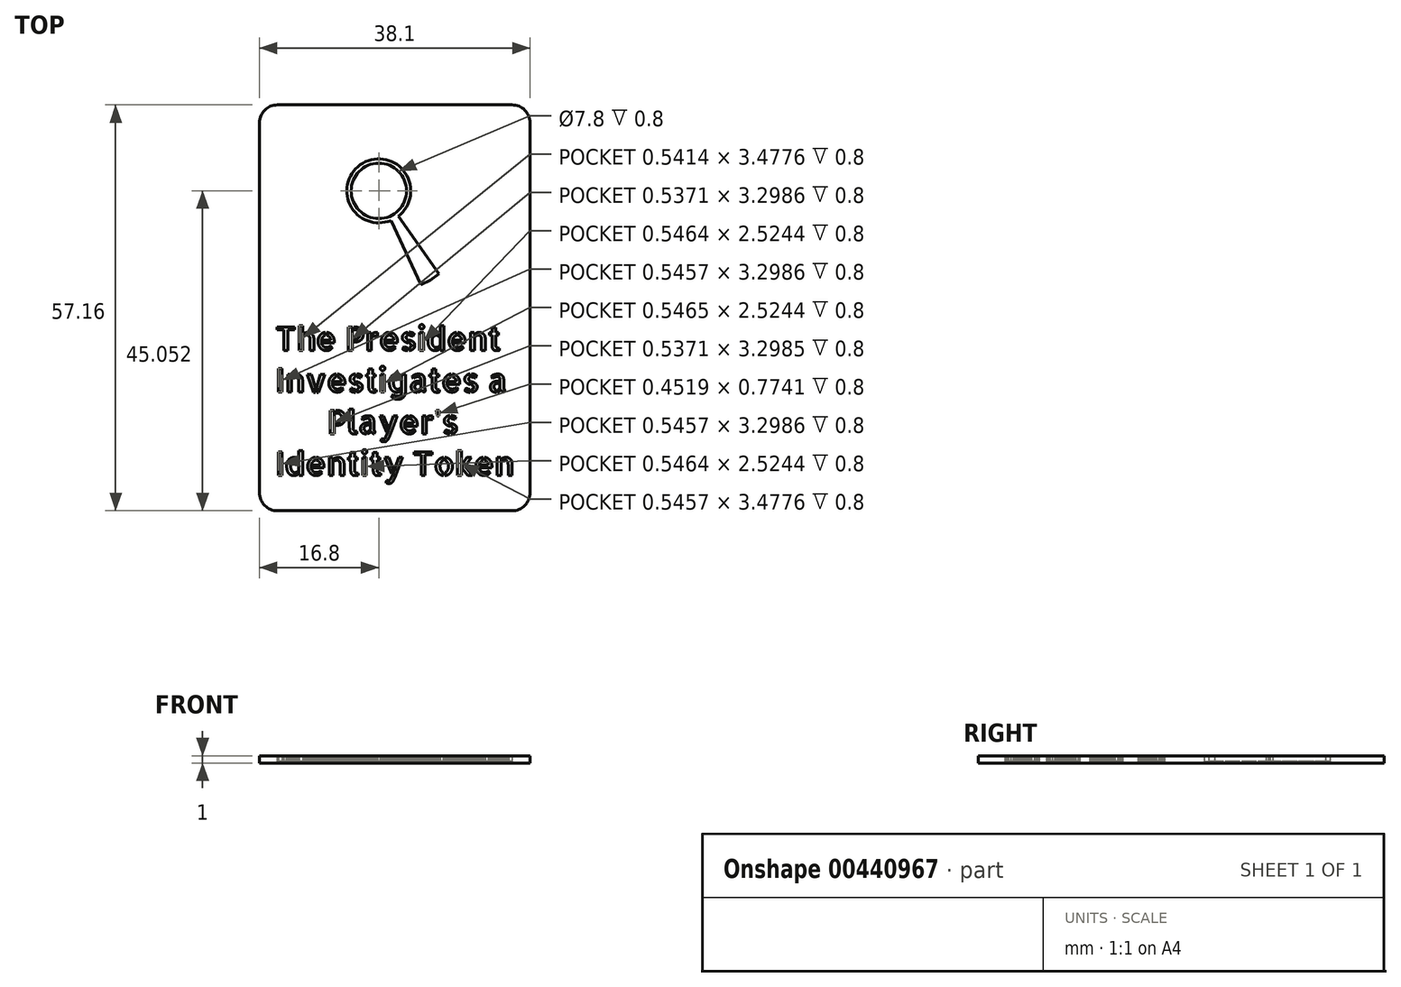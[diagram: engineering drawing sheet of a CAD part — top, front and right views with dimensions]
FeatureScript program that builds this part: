
annotation { "Feature Type Name" : "Feature", "Feature Type Description" : "" }
export const myFeature = defineFeature(function(context is Context, id is Id, definition is map)
    precondition{}
    {
        {
            var Q0;
            Q0=qCreatedBy(makeId("Top.planeOp"),FACE);
            var sketch = newSketch(context, id + "F0", { "sketchPlane" : qUnion([Q0])});
            skLineSegment(sketch, "E0.bottom", {"start": v(16.5, 28.58) * mm, "end": v(-16.51, 28.58) * mm});
            skLineSegment(sketch, "E0.top", {"start": v(16.51, -28.58) * mm, "end": v(-16.5, -28.58) * mm});
            skLineSegment(sketch, "E0.left", {"start": v(19.05, 26.04) * mm, "end": v(19.05, -26.04) * mm});
            skLineSegment(sketch, "E0.right", {"start": v(-19.05, 26.04) * mm, "end": v(-19.05, -26.04) * mm});
            skPoint(sketch, "E1.visualSharp", {"position": v(-19.05, 28.58) * mm});
            skArc(sketch, "E1.filletArc", {"start": v(-16.51, 28.58) * mm, "mid": v(-18.3, 27.83) * mm, "end": v(-19.05, 26.04) * mm});
            skPoint(sketch, "E2.visualSharp", {"position": v(19.05, 28.58) * mm});
            skArc(sketch, "E2.filletArc", {"start": v(19.05, 26.04) * mm, "mid": v(18.3, 27.83) * mm, "end": v(16.5, 28.58) * mm});
            skPoint(sketch, "E3.visualSharp", {"position": v(19.05, -28.58) * mm});
            skArc(sketch, "E3.filletArc", {"start": v(16.51, -28.58) * mm, "mid": v(18.3, -27.83) * mm, "end": v(19.05, -26.04) * mm});
            skPoint(sketch, "E4.visualSharp", {"position": v(-19.05, -28.58) * mm});
            skArc(sketch, "E4.filletArc", {"start": v(-19.05, -26.04) * mm, "mid": v(-18.3, -27.83) * mm, "end": v(-16.5, -28.58) * mm});
            skPoint(sketch, "E5", {"position": v(0, 12.58) * mm});
            skLineSegment(sketch, "E6", {"start": v(0, 12.58) * mm, "end": v(-19.05, 12.58) * mm, "construction": true});
            skLineSegment(sketch, "E7", {"start": v(0, 12.58) * mm, "end": v(19.05, 12.58) * mm, "construction": true});
            skLineSegment(sketch, "E8", {"start": v(0, 28.58) * mm, "end": v(0, 0) * mm, "construction": true});
            skLineSegment(sketch, "E9", {"start": v(0, 0) * mm, "end": v(0, -28.58) * mm, "construction": true});
            skCircle(sketch, "E10", {"center": v(-2.25, 16.47) * mm, "radius": 4.5 * mm});
            skCircle(sketch, "E11.0", {"center": v(-2.25, 16.47) * mm, "radius": 3.9 * mm});
            skLineSegment(sketch, "E12", {"start": v(-2.25, 16.47) * mm, "end": v(7.26, 0) * mm, "construction": true});
            skLineSegment(sketch, "E13", {"start": v(0.5, 12.9) * mm, "end": v(6.2, 4.76) * mm});
            skLineSegment(sketch, "E14", {"start": v(6.2, 4.76) * mm, "end": v(5, 3.91) * mm});
            skLineSegment(sketch, "E15.MirrorCS", {"start": v(-0.54, 12.31) * mm, "end": v(3.67, 3.3) * mm});
            skLineSegment(sketch, "E16.MirrorCS", {"start": v(3.67, 3.3) * mm, "end": v(5, 3.91) * mm});
            skText(sketch, "E17", { "text": "The President\nInvestigates a\n      Player\'s \nIdentity Token", "fontName": "AllertaStencil-Regular.ttf"});
            skLineSegment(sketch, "E18", {"start": v(-16.83, -2.7) * mm, "end": v(-19.05, -2.7) * mm, "construction": true});
            skLineSegment(sketch, "E19", {"start": v(16.83, -2.7) * mm, "end": v(19.05, -2.7) * mm, "construction": true});
            const initialGuessF0  = {"E17": [-0.01683, -0.006, 1, 0, 0.0033]};
            skSetInitialGuess(sketch, initialGuessF0);
            skSolve(sketch);
        }
        {
            var Q0;
            Q0=qSketchRegion(id+"F0",true);
            var Q1;
            Q1=makeQuery(id+"F0.imprint","IMPRINT",FACE,{"disambiguationData":[TD([[makeQuery(id+"F0.imprint","IMPRINT",EDGE,{"derivedFrom":sQuery(id+"F0.wireOp",EDGE,"1hngZ8Vo-O2Y1-8GoF-9924-SmxzgvlIe6eu")}),1.0]])]});
            var Q2;
            Q2=makeQuery(id+"F0.imprint","IMPRINT",FACE,{"disambiguationData":[TD([[makeQuery(id+"F0.imprint","IMPRINT",EDGE,{"derivedFrom":sQuery(id+"F0.wireOp",EDGE,"v3mnc92D-8hCO-dKtl-YXU8-LdhrgQy31VMY")}),1.0]])]});
            var Q3;
            Q3=makeQuery(id+"F0.imprint","IMPRINT",FACE,{"disambiguationData":[TD([[makeQuery(id+"F0.imprint","IMPRINT",EDGE,{"derivedFrom":sQuery(id+"F0.wireOp",EDGE,"XZppkLhH-C5au-Wygf-dwhr-iVVlCesrx2pO")}),1.0]])]});
            var Q4;
            Q4=makeQuery(id+"F0.imprint","IMPRINT",FACE,{"disambiguationData":[TD([[makeQuery(id+"F0.imprint","IMPRINT",EDGE,{"derivedFrom":sQuery(id+"F0.wireOp",EDGE,"y07g3fre-KKaQ-oYPB-yLvA-0BrsEIY3R70T")}),1.0]])]});
            var Q5;
            Q5=makeQuery(id+"F0.imprint","IMPRINT",FACE,{"disambiguationData":[TD([[makeQuery(id+"F0.imprint","IMPRINT",EDGE,{"derivedFrom":sQuery(id+"F0.wireOp",EDGE,"11e286c5-9b9c-43ac-b103-53d864957ac1.sketch_text.stroke-0")}),-1.0]])]});
            var Q6;
            Q6=makeQuery(id+"F0.imprint","IMPRINT",FACE,{"disambiguationData":[TD([[makeQuery(id+"F0.imprint","IMPRINT",EDGE,{"derivedFrom":sQuery(id+"F0.wireOp",EDGE,"11e286c5-9b9c-43ac-b103-53d864957ac1.sketch_text.stroke-8")}),-1.0]])]});
            var Q7;
            Q7=makeQuery(id+"F0.imprint","IMPRINT",FACE,{"disambiguationData":[TD([[makeQuery(id+"F0.imprint","IMPRINT",EDGE,{"derivedFrom":sQuery(id+"F0.wireOp",EDGE,"11e286c5-9b9c-43ac-b103-53d864957ac1.sketch_text.stroke-4")}),-1.0]])]});
            var Q8;
            Q8=makeQuery(id+"F0.imprint","IMPRINT",FACE,{"disambiguationData":[TD([[makeQuery(id+"F0.imprint","IMPRINT",EDGE,{"derivedFrom":sQuery(id+"F0.wireOp",EDGE,"11e286c5-9b9c-43ac-b103-53d864957ac1.sketch_text.stroke-31")}),-1.0]])]});
            var Q9;
            Q9=makeQuery(id+"F0.imprint","IMPRINT",FACE,{"disambiguationData":[TD([[makeQuery(id+"F0.imprint","IMPRINT",EDGE,{"derivedFrom":sQuery(id+"F0.wireOp",EDGE,"11e286c5-9b9c-43ac-b103-53d864957ac1.sketch_text.stroke-12")}),-1.0]])]});
            var Q10;
            Q10=makeQuery(id+"F0.imprint","IMPRINT",FACE,{"disambiguationData":[TD([[makeQuery(id+"F0.imprint","IMPRINT",EDGE,{"derivedFrom":sQuery(id+"F0.wireOp",EDGE,"11e286c5-9b9c-43ac-b103-53d864957ac1.sketch_text.stroke-96")}),-1.0]])]});
            var Q11;
            Q11=makeQuery(id+"F0.imprint","IMPRINT",FACE,{"disambiguationData":[TD([[makeQuery(id+"F0.imprint","IMPRINT",EDGE,{"derivedFrom":sQuery(id+"F0.wireOp",EDGE,"11e286c5-9b9c-43ac-b103-53d864957ac1.sketch_text.stroke-87")}),-1.0]])]});
            var Q12;
            Q12=makeQuery(id+"F0.imprint","IMPRINT",FACE,{"disambiguationData":[TD([[makeQuery(id+"F0.imprint","IMPRINT",EDGE,{"derivedFrom":sQuery(id+"F0.wireOp",EDGE,"11e286c5-9b9c-43ac-b103-53d864957ac1.sketch_text.stroke-67")}),-1.0]])]});
            var Q13;
            Q13=makeQuery(id+"F0.imprint","IMPRINT",FACE,{"disambiguationData":[TD([[makeQuery(id+"F0.imprint","IMPRINT",EDGE,{"derivedFrom":sQuery(id+"F0.wireOp",EDGE,"11e286c5-9b9c-43ac-b103-53d864957ac1.sketch_text.stroke-81")}),-1.0]])]});
            var Q14;
            Q14=makeQuery(id+"F0.imprint","IMPRINT",FACE,{"disambiguationData":[TD([[makeQuery(id+"F0.imprint","IMPRINT",EDGE,{"derivedFrom":sQuery(id+"F0.wireOp",EDGE,"11e286c5-9b9c-43ac-b103-53d864957ac1.sketch_text.stroke-116")}),-1.0]])]});
            var Q15;
            Q15=makeQuery(id+"F0.imprint","IMPRINT",FACE,{"disambiguationData":[TD([[makeQuery(id+"F0.imprint","IMPRINT",EDGE,{"derivedFrom":sQuery(id+"F0.wireOp",EDGE,"11e286c5-9b9c-43ac-b103-53d864957ac1.sketch_text.stroke-122")}),-1.0]])]});
            var Q16;
            Q16=makeQuery(id+"F0.imprint","IMPRINT",FACE,{"disambiguationData":[TD([[makeQuery(id+"F0.imprint","IMPRINT",EDGE,{"derivedFrom":sQuery(id+"F0.wireOp",EDGE,"11e286c5-9b9c-43ac-b103-53d864957ac1.sketch_text.stroke-110")}),-1.0]])]});
            var Q17;
            Q17=makeQuery(id+"F0.imprint","IMPRINT",FACE,{"disambiguationData":[TD([[makeQuery(id+"F0.imprint","IMPRINT",EDGE,{"derivedFrom":sQuery(id+"F0.wireOp",EDGE,"11e286c5-9b9c-43ac-b103-53d864957ac1.sketch_text.stroke-142")}),-1.0]])]});
            var Q18;
            Q18=makeQuery(id+"F0.imprint","IMPRINT",FACE,{"disambiguationData":[TD([[makeQuery(id+"F0.imprint","IMPRINT",EDGE,{"derivedFrom":sQuery(id+"F0.wireOp",EDGE,"11e286c5-9b9c-43ac-b103-53d864957ac1.sketch_text.stroke-138")}),-1.0]])]});
            var Q19;
            Q19=makeQuery(id+"F0.imprint","IMPRINT",FACE,{"disambiguationData":[TD([[makeQuery(id+"F0.imprint","IMPRINT",EDGE,{"derivedFrom":sQuery(id+"F0.wireOp",EDGE,"11e286c5-9b9c-43ac-b103-53d864957ac1.sketch_text.stroke-170")}),-1.0]])]});
            var Q20;
            Q20=makeQuery(id+"F0.imprint","IMPRINT",FACE,{"disambiguationData":[TD([[makeQuery(id+"F0.imprint","IMPRINT",EDGE,{"derivedFrom":sQuery(id+"F0.wireOp",EDGE,"11e286c5-9b9c-43ac-b103-53d864957ac1.sketch_text.stroke-179")}),-1.0]])]});
            var Q21;
            Q21=makeQuery(id+"F0.imprint","IMPRINT",FACE,{"disambiguationData":[TD([[makeQuery(id+"F0.imprint","IMPRINT",EDGE,{"derivedFrom":sQuery(id+"F0.wireOp",EDGE,"11e286c5-9b9c-43ac-b103-53d864957ac1.sketch_text.stroke-150")}),-1.0]])]});
            var Q22;
            Q22=makeQuery(id+"F0.imprint","IMPRINT",FACE,{"disambiguationData":[TD([[makeQuery(id+"F0.imprint","IMPRINT",EDGE,{"derivedFrom":sQuery(id+"F0.wireOp",EDGE,"11e286c5-9b9c-43ac-b103-53d864957ac1.sketch_text.stroke-164")}),-1.0]])]});
            var Q23;
            Q23=makeQuery(id+"F0.imprint","IMPRINT",FACE,{"disambiguationData":[TD([[makeQuery(id+"F0.imprint","IMPRINT",EDGE,{"derivedFrom":sQuery(id+"F0.wireOp",EDGE,"11e286c5-9b9c-43ac-b103-53d864957ac1.sketch_text.stroke-193")}),-1.0]])]});
            var Q24;
            Q24=makeQuery(id+"F0.imprint","IMPRINT",FACE,{"disambiguationData":[TD([[makeQuery(id+"F0.imprint","IMPRINT",EDGE,{"derivedFrom":sQuery(id+"F0.wireOp",EDGE,"3hOEF64v-dSEU-imgf-cV2M-oAy4Y8LvNKR4")}),1.0]])]});
            var Q25;
            Q25=makeQuery(id+"F0.imprint","IMPRINT",FACE,{"disambiguationData":[TD([[makeQuery(id+"F0.imprint","IMPRINT",EDGE,{"derivedFrom":sQuery(id+"F0.wireOp",EDGE,"d61e87b4-afbc-4eba-b1e1-6c312846f633.1.0.0")}),1.0]])]});
            var Q26;
            Q26=makeQuery(id+"F0.imprint","IMPRINT",FACE,{"disambiguationData":[TD([[makeQuery(id+"F0.imprint","IMPRINT",EDGE,{"derivedFrom":sQuery(id+"F0.wireOp",EDGE,"d61e87b4-afbc-4eba-b1e1-6c312846f633.2.0.0")}),1.0]])]});
            var Q27;
            Q27=makeQuery(id+"F0.imprint","IMPRINT",FACE,{"disambiguationData":[TD([[makeQuery(id+"F0.imprint","IMPRINT",EDGE,{"derivedFrom":sQuery(id+"F0.wireOp",EDGE,"d61e87b4-afbc-4eba-b1e1-6c312846f633.3.0.0")}),1.0]])]});
            var Q28;
            Q28=makeQuery(id+"F0.imprint","IMPRINT",FACE,{"disambiguationData":[TD([[makeQuery(id+"F0.imprint","IMPRINT",EDGE,{"derivedFrom":sQuery(id+"F0.wireOp",EDGE,"d61e87b4-afbc-4eba-b1e1-6c312846f633.4.0.0")}),1.0]])]});
            var Q29;
            Q29=makeQuery(id+"F0.imprint","IMPRINT",FACE,{"disambiguationData":[TD([[makeQuery(id+"F0.imprint","IMPRINT",EDGE,{"derivedFrom":sQuery(id+"F0.wireOp",EDGE,"d61e87b4-afbc-4eba-b1e1-6c312846f633.5.0.0")}),1.0]])]});
            var Q30;
            Q30=makeQuery(id+"F0.imprint","IMPRINT",FACE,{"disambiguationData":[TD([[makeQuery(id+"F0.imprint","IMPRINT",EDGE,{"derivedFrom":sQuery(id+"F0.wireOp",EDGE,"d61e87b4-afbc-4eba-b1e1-6c312846f633.6.0.0")}),1.0]])]});
            var Q31;
            Q31=makeQuery(id+"F0.imprint","IMPRINT",FACE,{"disambiguationData":[TD([[makeQuery(id+"F0.imprint","IMPRINT",EDGE,{"derivedFrom":sQuery(id+"F0.wireOp",EDGE,"d61e87b4-afbc-4eba-b1e1-6c312846f633.7.0.0")}),1.0]])]});
            var Q32;
            Q32=makeQuery(id+"F0.imprint","IMPRINT",FACE,{"disambiguationData":[TD([[makeQuery(id+"F0.imprint","IMPRINT",EDGE,{"derivedFrom":sQuery(id+"F0.wireOp",EDGE,"d61e87b4-afbc-4eba-b1e1-6c312846f633.8.0.0")}),1.0]])]});
            var Q33;
            Q33=makeQuery(id+"F0.imprint","IMPRINT",FACE,{"disambiguationData":[TD([[makeQuery(id+"F0.imprint","IMPRINT",EDGE,{"derivedFrom":sQuery(id+"F0.wireOp",EDGE,"d61e87b4-afbc-4eba-b1e1-6c312846f633.9.0.0")}),1.0]])]});
            var Q34;
            Q34=makeQuery(id+"F0.imprint","IMPRINT",FACE,{"disambiguationData":[TD([[makeQuery(id+"F0.imprint","IMPRINT",EDGE,{"derivedFrom":sQuery(id+"F0.wireOp",EDGE,"d61e87b4-afbc-4eba-b1e1-6c312846f633.10.0.0")}),1.0]])]});
            var Q35;
            Q35=makeQuery(id+"F0.imprint","IMPRINT",FACE,{"disambiguationData":[TD([[makeQuery(id+"F0.imprint","IMPRINT",EDGE,{"derivedFrom":sQuery(id+"F0.wireOp",EDGE,"d61e87b4-afbc-4eba-b1e1-6c312846f633.11.0.0")}),1.0]])]});
            var Q36;
            Q36=makeQuery(id+"F0.imprint","IMPRINT",FACE,{"disambiguationData":[TD([[makeQuery(id+"F0.imprint","IMPRINT",EDGE,{"derivedFrom":sQuery(id+"F0.wireOp",EDGE,"d61e87b4-afbc-4eba-b1e1-6c312846f633.12.0.0")}),1.0]])]});
            var Q37;
            Q37=makeQuery(id+"F0.imprint","IMPRINT",FACE,{"disambiguationData":[TD([[makeQuery(id+"F0.imprint","IMPRINT",EDGE,{"derivedFrom":sQuery(id+"F0.wireOp",EDGE,"d61e87b4-afbc-4eba-b1e1-6c312846f633.13.0.0")}),1.0]])]});
            var Q38;
            Q38=makeQuery(id+"F0.imprint","IMPRINT",FACE,{"disambiguationData":[TD([[makeQuery(id+"F0.imprint","IMPRINT",EDGE,{"derivedFrom":sQuery(id+"F0.wireOp",EDGE,"d61e87b4-afbc-4eba-b1e1-6c312846f633.14.0.0")}),1.0]])]});
            var Q39;
            Q39=makeQuery(id+"F0.imprint","IMPRINT",FACE,{"disambiguationData":[TD([[makeQuery(id+"F0.imprint","IMPRINT",EDGE,{"derivedFrom":sQuery(id+"F0.wireOp",EDGE,"d61e87b4-afbc-4eba-b1e1-6c312846f633.15.0.0")}),1.0]])]});
            var Q40;
            Q40=makeQuery(id+"F0.imprint","IMPRINT",FACE,{"disambiguationData":[TD([[makeQuery(id+"F0.imprint","IMPRINT",EDGE,{"derivedFrom":sQuery(id+"F0.wireOp",EDGE,"d61e87b4-afbc-4eba-b1e1-6c312846f633.16.0.0")}),1.0]])]});
            var Q41;
            Q41=makeQuery(id+"F0.imprint","IMPRINT",FACE,{"disambiguationData":[TD([[makeQuery(id+"F0.imprint","IMPRINT",EDGE,{"derivedFrom":sQuery(id+"F0.wireOp",EDGE,"d61e87b4-afbc-4eba-b1e1-6c312846f633.17.0.0")}),1.0]])]});
            var Q42;
            Q42=makeQuery(id+"F0.imprint","IMPRINT",FACE,{"disambiguationData":[TD([[makeQuery(id+"F0.imprint","IMPRINT",EDGE,{"derivedFrom":sQuery(id+"F0.wireOp",EDGE,"d61e87b4-afbc-4eba-b1e1-6c312846f633.18.0.0")}),1.0]])]});
            var Q43;
            Q43=makeQuery(id+"F0.imprint","IMPRINT",FACE,{"disambiguationData":[TD([[makeQuery(id+"F0.imprint","IMPRINT",EDGE,{"derivedFrom":sQuery(id+"F0.wireOp",EDGE,"d61e87b4-afbc-4eba-b1e1-6c312846f633.19.0.0")}),1.0]])]});
            var Q44;
            Q44=makeQuery(id+"F0.imprint","IMPRINT",FACE,{"disambiguationData":[TD([[makeQuery(id+"F0.imprint","IMPRINT",EDGE,{"derivedFrom":sQuery(id+"F0.wireOp",EDGE,"d61e87b4-afbc-4eba-b1e1-6c312846f633.20.0.0")}),1.0]])]});
            var Q45;
            Q45=makeQuery(id+"F0.imprint","IMPRINT",FACE,{"disambiguationData":[TD([[makeQuery(id+"F0.imprint","IMPRINT",EDGE,{"derivedFrom":sQuery(id+"F0.wireOp",EDGE,"d61e87b4-afbc-4eba-b1e1-6c312846f633.21.0.0")}),1.0]])]});
            var Q46;
            Q46=makeQuery(id+"F0.imprint","IMPRINT",FACE,{"disambiguationData":[TD([[makeQuery(id+"F0.imprint","IMPRINT",EDGE,{"derivedFrom":sQuery(id+"F0.wireOp",EDGE,"824da2b7-0e67-4436-b530-e222e440d070.sketch_text.stroke-0")}),-1.0]])]});
            var Q47;
            Q47=makeQuery(id+"F0.imprint","IMPRINT",FACE,{"disambiguationData":[TD([[makeQuery(id+"F0.imprint","IMPRINT",EDGE,{"derivedFrom":sQuery(id+"F0.wireOp",EDGE,"824da2b7-0e67-4436-b530-e222e440d070.sketch_text.stroke-15")}),-1.0]])]});
            var Q48;
            Q48=makeQuery(id+"F0.imprint","IMPRINT",FACE,{"disambiguationData":[TD([[makeQuery(id+"F0.imprint","IMPRINT",EDGE,{"derivedFrom":sQuery(id+"F0.wireOp",EDGE,"824da2b7-0e67-4436-b530-e222e440d070.sketch_text.stroke-32")}),-1.0]])]});
            var Q49;
            Q49=makeQuery(id+"F0.imprint","IMPRINT",FACE,{"disambiguationData":[TD([[makeQuery(id+"F0.imprint","IMPRINT",EDGE,{"derivedFrom":sQuery(id+"F0.wireOp",EDGE,"824da2b7-0e67-4436-b530-e222e440d070.sketch_text.stroke-54")}),-1.0]])]});
            var Q50;
            Q50=makeQuery(id+"F0.imprint","IMPRINT",FACE,{"disambiguationData":[TD([[makeQuery(id+"F0.imprint","IMPRINT",EDGE,{"derivedFrom":sQuery(id+"F0.wireOp",EDGE,"824da2b7-0e67-4436-b530-e222e440d070.sketch_text.stroke-50")}),-1.0]])]});
            var Q51;
            Q51=makeQuery(id+"F0.imprint","IMPRINT",FACE,{"disambiguationData":[TD([[makeQuery(id+"F0.imprint","IMPRINT",EDGE,{"derivedFrom":sQuery(id+"F0.wireOp",EDGE,"824da2b7-0e67-4436-b530-e222e440d070.sketch_text.stroke-58")}),-1.0]])]});
            var Q52;
            Q52=makeQuery(id+"F0.imprint","IMPRINT",FACE,{"disambiguationData":[TD([[makeQuery(id+"F0.imprint","IMPRINT",EDGE,{"derivedFrom":sQuery(id+"F0.wireOp",EDGE,"824da2b7-0e67-4436-b530-e222e440d070.sketch_text.stroke-75")}),-1.0]])]});
            var Q53;
            Q53=makeQuery(id+"F0.imprint","IMPRINT",FACE,{"disambiguationData":[TD([[makeQuery(id+"F0.imprint","IMPRINT",EDGE,{"derivedFrom":sQuery(id+"F0.wireOp",EDGE,"824da2b7-0e67-4436-b530-e222e440d070.sketch_text.stroke-79")}),-1.0]])]});
            var Q54;
            Q54=makeQuery(id+"F0.imprint","IMPRINT",FACE,{"disambiguationData":[TD([[makeQuery(id+"F0.imprint","IMPRINT",EDGE,{"derivedFrom":sQuery(id+"F0.wireOp",EDGE,"prHT7NwA-CJht-v5NG-W2o7-Xqmxs18joHLs.bottom")}),-1.0]])]});
            var Q55;
            Q55=makeQuery(id+"F0.imprint","IMPRINT",FACE,{"disambiguationData":[TD([[makeQuery(id+"F0.imprint","IMPRINT",EDGE,{"derivedFrom":sQuery(id+"F0.wireOp",EDGE,"loqv97KZ-vKno-A8WI-mPE9-OnQyIJFUs6ra.bottom")}),-1.0]])]});
            var Q56;
            Q56=makeQuery(id+"F0.imprint","IMPRINT",FACE,{"disambiguationData":[TD([[makeQuery(id+"F0.imprint","IMPRINT",EDGE,{"derivedFrom":sQuery(id+"F0.wireOp",EDGE,"IiW4FtL9-cIlY-GVfC-fHN8-Muj6rfwzQ4Nk.bottom")}),-1.0]])]});
            var Q57;
            Q57=makeQuery(id+"F0.imprint","IMPRINT",FACE,{"disambiguationData":[TD([[makeQuery(id+"F0.imprint","IMPRINT",EDGE,{"derivedFrom":sQuery(id+"F0.wireOp",EDGE,"hgyYalZY-fuKV-cGhY-Ue2A-NU4bW9GvdhIw.bottom")}),-1.0]])]});
            var Q58;
            Q58=makeQuery(id+"F0.imprint","IMPRINT",FACE,{"disambiguationData":[TD([[makeQuery(id+"F0.imprint","IMPRINT",EDGE,{"derivedFrom":sQuery(id+"F0.wireOp",EDGE,"7RaPNTs9-LwY4-UvGH-fbjw-P0gIc8EvOOef.bottom")}),-1.0]])]});
            var Q59;
            Q59=makeQuery(id+"F0.imprint","IMPRINT",FACE,{"disambiguationData":[TD([[makeQuery(id+"F0.imprint","IMPRINT",EDGE,{"derivedFrom":sQuery(id+"F0.wireOp",EDGE,"0Oy3iZBW-l60p-ye98-HsD0-8aETsZGMw3y6.bottom")}),-1.0]])]});
            var Q60;
            Q60=makeQuery(id+"F0.imprint","IMPRINT",FACE,{"disambiguationData":[TD([[makeQuery(id+"F0.imprint","IMPRINT",EDGE,{"derivedFrom":sQuery(id+"F0.wireOp",EDGE,"uO9PoV1c-vtol-dT46-PGAY-6wPjbnXBpNAn.bottom")}),-1.0]])]});
            var Q61;
            Q61=makeQuery(id+"F0.imprint","IMPRINT",FACE,{"disambiguationData":[TD([[makeQuery(id+"F0.imprint","IMPRINT",EDGE,{"derivedFrom":sQuery(id+"F0.wireOp",EDGE,"HzYubSo2-mYeH-qRyi-21AG-W6rulPkjMyM9.bottom")}),-1.0]])]});
            var Q62;
            Q62=makeQuery(id+"F0.imprint","IMPRINT",FACE,{"disambiguationData":[TD([[makeQuery(id+"F0.imprint","IMPRINT",EDGE,{"derivedFrom":sQuery(id+"F0.wireOp",EDGE,"E11.0")}),1.0]])]});
            extrude(context, id + "F1", {"entities" : qUnion([Q0, Q1, Q2, Q3, Q4, Q5, Q6, Q7, Q8, Q9, Q10, Q11, Q12, Q13, Q14, Q15, Q16, Q17, Q18, Q19, Q20, Q21, Q22, Q23, Q24, Q25, Q26, Q27, Q28, Q29, Q30, Q31, Q32, Q33, Q34, Q35, Q36, Q37, Q38, Q39, Q40, Q41, Q42, Q43, Q44, Q45, Q46, Q47, Q48, Q49, Q50, Q51, Q52, Q53, Q54, Q55, Q56, Q57, Q58, Q59, Q60, Q61, Q62]), "depth" : 1 * mm, "offsetDistance" : 25 * mm});
        }
        {
            var Q0;
            Q0=makeQuery(id+"F0.imprint","IMPRINT",FACE,{"disambiguationData":[TD([[makeQuery(id+"F0.imprint","IMPRINT",EDGE,{"derivedFrom":sQuery(id+"F0.wireOp",EDGE,"E17.sketch_text.stroke-200")}),-1.0]])]});
            var Q1;
            Q1=makeQuery(id+"F0.imprint","IMPRINT",FACE,{"disambiguationData":[TD([[makeQuery(id+"F0.imprint","IMPRINT",EDGE,{"derivedFrom":sQuery(id+"F0.wireOp",EDGE,"E17.sketch_text.stroke-192")}),-1.0]])]});
            var Q2;
            Q2=makeQuery(id+"F0.imprint","IMPRINT",FACE,{"disambiguationData":[TD([[makeQuery(id+"F0.imprint","IMPRINT",EDGE,{"derivedFrom":sQuery(id+"F0.wireOp",EDGE,"E17.sketch_text.stroke-291")}),-1.0]])]});
            var Q3;
            {var subQ0=sQuery(id+"F0.wireOp",EDGE,"E13");Q3=makeQuery(id+"F0.imprint","IMPRINT",FACE,{"disambiguationData":[TD([[makeQuery(id+"F0.imprint","IMPRINT",EDGE,{"derivedFrom":subQ0}),-1.0]])]});}
            var Q4;
            Q4=makeQuery(id+"F0.imprint","IMPRINT",FACE,{"disambiguationData":[TD([[makeQuery(id+"F0.imprint","IMPRINT",EDGE,{"derivedFrom":sQuery(id+"F0.wireOp",EDGE,"E11.0")}),-1.0]])]});
            var Q5;
            Q5=makeQuery(id+"F0.imprint","IMPRINT",FACE,{"disambiguationData":[TD([[makeQuery(id+"F0.imprint","IMPRINT",EDGE,{"derivedFrom":sQuery(id+"F0.wireOp",EDGE,"E17.sketch_text.stroke-870")}),-1.0]])]});
            var Q6;
            Q6=makeQuery(id+"F0.imprint","IMPRINT",FACE,{"disambiguationData":[TD([[makeQuery(id+"F0.imprint","IMPRINT",EDGE,{"derivedFrom":sQuery(id+"F0.wireOp",EDGE,"E17.sketch_text.stroke-101")}),-1.0]])]});
            var Q7;
            Q7=makeQuery(id+"F0.imprint","IMPRINT",FACE,{"disambiguationData":[TD([[makeQuery(id+"F0.imprint","IMPRINT",EDGE,{"derivedFrom":sQuery(id+"F0.wireOp",EDGE,"E17.sketch_text.stroke-145")}),-1.0]])]});
            var Q8;
            Q8=makeQuery(id+"F0.imprint","IMPRINT",FACE,{"disambiguationData":[TD([[makeQuery(id+"F0.imprint","IMPRINT",EDGE,{"derivedFrom":sQuery(id+"F0.wireOp",EDGE,"E17.sketch_text.stroke-68")}),-1.0]])]});
            var Q9;
            Q9=makeQuery(id+"F0.imprint","IMPRINT",FACE,{"disambiguationData":[TD([[makeQuery(id+"F0.imprint","IMPRINT",EDGE,{"derivedFrom":sQuery(id+"F0.wireOp",EDGE,"E17.sketch_text.stroke-108")}),-1.0]])]});
            var Q10;
            Q10=makeQuery(id+"F0.imprint","IMPRINT",FACE,{"disambiguationData":[TD([[makeQuery(id+"F0.imprint","IMPRINT",EDGE,{"derivedFrom":sQuery(id+"F0.wireOp",EDGE,"E17.sketch_text.stroke-121")}),-1.0]])]});
            var Q11;
            Q11=makeQuery(id+"F0.imprint","IMPRINT",FACE,{"disambiguationData":[TD([[makeQuery(id+"F0.imprint","IMPRINT",EDGE,{"derivedFrom":sQuery(id+"F0.wireOp",EDGE,"E17.sketch_text.stroke-94")}),-1.0]])]});
            var Q12;
            Q12=makeQuery(id+"F0.imprint","IMPRINT",FACE,{"disambiguationData":[TD([[makeQuery(id+"F0.imprint","IMPRINT",EDGE,{"derivedFrom":sQuery(id+"F0.wireOp",EDGE,"E17.sketch_text.stroke-72")}),-1.0]])]});
            var Q13;
            Q13=makeQuery(id+"F0.imprint","IMPRINT",FACE,{"disambiguationData":[TD([[makeQuery(id+"F0.imprint","IMPRINT",EDGE,{"derivedFrom":sQuery(id+"F0.wireOp",EDGE,"E17.sketch_text.stroke-1079")}),-1.0]])]});
            var Q14;
            Q14=makeQuery(id+"F0.imprint","IMPRINT",FACE,{"disambiguationData":[TD([[makeQuery(id+"F0.imprint","IMPRINT",EDGE,{"derivedFrom":sQuery(id+"F0.wireOp",EDGE,"E17.sketch_text.stroke-205")}),-1.0]])]});
            var Q15;
            Q15=makeQuery(id+"F0.imprint","IMPRINT",FACE,{"disambiguationData":[TD([[makeQuery(id+"F0.imprint","IMPRINT",EDGE,{"derivedFrom":sQuery(id+"F0.wireOp",EDGE,"E17.sketch_text.stroke-941")}),-1.0]])]});
            var Q16;
            Q16=makeQuery(id+"F0.imprint","IMPRINT",FACE,{"disambiguationData":[TD([[makeQuery(id+"F0.imprint","IMPRINT",EDGE,{"derivedFrom":sQuery(id+"F0.wireOp",EDGE,"E17.sketch_text.stroke-792")}),-1.0]])]});
            var Q17;
            Q17=makeQuery(id+"F0.imprint","IMPRINT",FACE,{"disambiguationData":[TD([[makeQuery(id+"F0.imprint","IMPRINT",EDGE,{"derivedFrom":sQuery(id+"F0.wireOp",EDGE,"E17.sketch_text.stroke-1031")}),-1.0]])]});
            var Q18;
            Q18=makeQuery(id+"F0.imprint","IMPRINT",FACE,{"disambiguationData":[TD([[makeQuery(id+"F0.imprint","IMPRINT",EDGE,{"derivedFrom":sQuery(id+"F0.wireOp",EDGE,"E17.sketch_text.stroke-857")}),-1.0]])]});
            var Q19;
            Q19=makeQuery(id+"F0.imprint","IMPRINT",FACE,{"disambiguationData":[TD([[makeQuery(id+"F0.imprint","IMPRINT",EDGE,{"derivedFrom":sQuery(id+"F0.wireOp",EDGE,"E17.sketch_text.stroke-569")}),-1.0]])]});
            var Q20;
            Q20=makeQuery(id+"F0.imprint","IMPRINT",FACE,{"disambiguationData":[TD([[makeQuery(id+"F0.imprint","IMPRINT",EDGE,{"derivedFrom":sQuery(id+"F0.wireOp",EDGE,"E17.sketch_text.stroke-325")}),-1.0]])]});
            var Q21;
            Q21=makeQuery(id+"F0.imprint","IMPRINT",FACE,{"disambiguationData":[TD([[makeQuery(id+"F0.imprint","IMPRINT",EDGE,{"derivedFrom":sQuery(id+"F0.wireOp",EDGE,"E17.sketch_text.stroke-1050")}),-1.0]])]});
            var Q22;
            Q22=makeQuery(id+"F0.imprint","IMPRINT",FACE,{"disambiguationData":[TD([[makeQuery(id+"F0.imprint","IMPRINT",EDGE,{"derivedFrom":sQuery(id+"F0.wireOp",EDGE,"E17.sketch_text.stroke-594")}),-1.0]])]});
            var Q23;
            Q23=makeQuery(id+"F0.imprint","IMPRINT",FACE,{"disambiguationData":[TD([[makeQuery(id+"F0.imprint","IMPRINT",EDGE,{"derivedFrom":sQuery(id+"F0.wireOp",EDGE,"E17.sketch_text.stroke-344")}),-1.0]])]});
            var Q24;
            Q24=makeQuery(id+"F0.imprint","IMPRINT",FACE,{"disambiguationData":[TD([[makeQuery(id+"F0.imprint","IMPRINT",EDGE,{"derivedFrom":sQuery(id+"F0.wireOp",EDGE,"E17.sketch_text.stroke-1075")}),-1.0]])]});
            var Q25;
            Q25=makeQuery(id+"F0.imprint","IMPRINT",FACE,{"disambiguationData":[TD([[makeQuery(id+"F0.imprint","IMPRINT",EDGE,{"derivedFrom":sQuery(id+"F0.wireOp",EDGE,"E17.sketch_text.stroke-174")}),-1.0]])]});
            var Q26;
            Q26=makeQuery(id+"F0.imprint","IMPRINT",FACE,{"disambiguationData":[TD([[makeQuery(id+"F0.imprint","IMPRINT",EDGE,{"derivedFrom":sQuery(id+"F0.wireOp",EDGE,"E17.sketch_text.stroke-159")}),-1.0]])]});
            var Q27;
            Q27=makeQuery(id+"F0.imprint","IMPRINT",FACE,{"disambiguationData":[TD([[makeQuery(id+"F0.imprint","IMPRINT",EDGE,{"derivedFrom":sQuery(id+"F0.wireOp",EDGE,"E17.sketch_text.stroke-165")}),-1.0]])]});
            var Q28;
            Q28=makeQuery(id+"F0.imprint","IMPRINT",FACE,{"disambiguationData":[TD([[makeQuery(id+"F0.imprint","IMPRINT",EDGE,{"derivedFrom":sQuery(id+"F0.wireOp",EDGE,"E17.sketch_text.stroke-0")}),-1.0]])]});
            var Q29;
            Q29=makeQuery(id+"F0.imprint","IMPRINT",FACE,{"disambiguationData":[TD([[makeQuery(id+"F0.imprint","IMPRINT",EDGE,{"derivedFrom":sQuery(id+"F0.wireOp",EDGE,"E17.sketch_text.stroke-8")}),-1.0]])]});
            var Q30;
            Q30=makeQuery(id+"F0.imprint","IMPRINT",FACE,{"disambiguationData":[TD([[makeQuery(id+"F0.imprint","IMPRINT",EDGE,{"derivedFrom":sQuery(id+"F0.wireOp",EDGE,"E17.sketch_text.stroke-12")}),-1.0]])]});
            var Q31;
            Q31=makeQuery(id+"F0.imprint","IMPRINT",FACE,{"disambiguationData":[TD([[makeQuery(id+"F0.imprint","IMPRINT",EDGE,{"derivedFrom":sQuery(id+"F0.wireOp",EDGE,"E17.sketch_text.stroke-31")}),-1.0]])]});
            var Q32;
            Q32=makeQuery(id+"F0.imprint","IMPRINT",FACE,{"disambiguationData":[TD([[makeQuery(id+"F0.imprint","IMPRINT",EDGE,{"derivedFrom":sQuery(id+"F0.wireOp",EDGE,"E17.sketch_text.stroke-44")}),-1.0]])]});
            var Q33;
            Q33=makeQuery(id+"F0.imprint","IMPRINT",FACE,{"disambiguationData":[TD([[makeQuery(id+"F0.imprint","IMPRINT",EDGE,{"derivedFrom":sQuery(id+"F0.wireOp",EDGE,"E17.sketch_text.stroke-367")}),-1.0]])]});
            var Q34;
            Q34=makeQuery(id+"F0.imprint","IMPRINT",FACE,{"disambiguationData":[TD([[makeQuery(id+"F0.imprint","IMPRINT",EDGE,{"derivedFrom":sQuery(id+"F0.wireOp",EDGE,"E17.sketch_text.stroke-1112")}),-1.0]])]});
            var Q35;
            Q35=makeQuery(id+"F0.imprint","IMPRINT",FACE,{"disambiguationData":[TD([[makeQuery(id+"F0.imprint","IMPRINT",EDGE,{"derivedFrom":sQuery(id+"F0.wireOp",EDGE,"E17.sketch_text.stroke-645")}),-1.0]])]});
            var Q36;
            Q36=makeQuery(id+"F0.imprint","IMPRINT",FACE,{"disambiguationData":[TD([[makeQuery(id+"F0.imprint","IMPRINT",EDGE,{"derivedFrom":sQuery(id+"F0.wireOp",EDGE,"E17.sketch_text.stroke-894")}),-1.0]])]});
            var Q37;
            Q37=makeQuery(id+"F0.imprint","IMPRINT",FACE,{"disambiguationData":[TD([[makeQuery(id+"F0.imprint","IMPRINT",EDGE,{"derivedFrom":sQuery(id+"F0.wireOp",EDGE,"E17.sketch_text.stroke-607")}),-1.0]])]});
            var Q38;
            Q38=makeQuery(id+"F0.imprint","IMPRINT",FACE,{"disambiguationData":[TD([[makeQuery(id+"F0.imprint","IMPRINT",EDGE,{"derivedFrom":sQuery(id+"F0.wireOp",EDGE,"E17.sketch_text.stroke-349")}),-1.0]])]});
            var Q39;
            Q39=makeQuery(id+"F0.imprint","IMPRINT",FACE,{"disambiguationData":[TD([[makeQuery(id+"F0.imprint","IMPRINT",EDGE,{"derivedFrom":sQuery(id+"F0.wireOp",EDGE,"E17.sketch_text.stroke-1087")}),-1.0]])]});
            var Q40;
            Q40=makeQuery(id+"F0.imprint","IMPRINT",FACE,{"disambiguationData":[TD([[makeQuery(id+"F0.imprint","IMPRINT",EDGE,{"derivedFrom":sQuery(id+"F0.wireOp",EDGE,"E17.sketch_text.stroke-901")}),-1.0]])]});
            var Q41;
            Q41=makeQuery(id+"F0.imprint","IMPRINT",FACE,{"disambiguationData":[TD([[makeQuery(id+"F0.imprint","IMPRINT",EDGE,{"derivedFrom":sQuery(id+"F0.wireOp",EDGE,"E17.sketch_text.stroke-631")}),-1.0]])]});
            var Q42;
            Q42=makeQuery(id+"F0.imprint","IMPRINT",FACE,{"disambiguationData":[TD([[makeQuery(id+"F0.imprint","IMPRINT",EDGE,{"derivedFrom":sQuery(id+"F0.wireOp",EDGE,"E17.sketch_text.stroke-354")}),-1.0]])]});
            var Q43;
            Q43=makeQuery(id+"F0.imprint","IMPRINT",FACE,{"disambiguationData":[TD([[makeQuery(id+"F0.imprint","IMPRINT",EDGE,{"derivedFrom":sQuery(id+"F0.wireOp",EDGE,"E17.sketch_text.stroke-188")}),-1.0]])]});
            var Q44;
            Q44=makeQuery(id+"F0.imprint","IMPRINT",FACE,{"disambiguationData":[TD([[makeQuery(id+"F0.imprint","IMPRINT",EDGE,{"derivedFrom":sQuery(id+"F0.wireOp",EDGE,"E17.sketch_text.stroke-1136")}),-1.0]])]});
            var Q45;
            Q45=makeQuery(id+"F0.imprint","IMPRINT",FACE,{"disambiguationData":[TD([[makeQuery(id+"F0.imprint","IMPRINT",EDGE,{"derivedFrom":sQuery(id+"F0.wireOp",EDGE,"E17.sketch_text.stroke-912")}),-1.0]])]});
            var Q46;
            Q46=makeQuery(id+"F0.imprint","IMPRINT",FACE,{"disambiguationData":[TD([[makeQuery(id+"F0.imprint","IMPRINT",EDGE,{"derivedFrom":sQuery(id+"F0.wireOp",EDGE,"E17.sketch_text.stroke-651")}),-1.0]])]});
            var Q47;
            Q47=makeQuery(id+"F0.imprint","IMPRINT",FACE,{"disambiguationData":[TD([[makeQuery(id+"F0.imprint","IMPRINT",EDGE,{"derivedFrom":sQuery(id+"F0.wireOp",EDGE,"E17.sketch_text.stroke-391")}),-1.0]])]});
            var Q48;
            Q48=makeQuery(id+"F0.imprint","IMPRINT",FACE,{"disambiguationData":[TD([[makeQuery(id+"F0.imprint","IMPRINT",EDGE,{"derivedFrom":sQuery(id+"F0.wireOp",EDGE,"E17.sketch_text.stroke-1141")}),-1.0]])]});
            var Q49;
            Q49=makeQuery(id+"F0.imprint","IMPRINT",FACE,{"disambiguationData":[TD([[makeQuery(id+"F0.imprint","IMPRINT",EDGE,{"derivedFrom":sQuery(id+"F0.wireOp",EDGE,"E17.sketch_text.stroke-926")}),-1.0]])]});
            var Q50;
            Q50=makeQuery(id+"F0.imprint","IMPRINT",FACE,{"disambiguationData":[TD([[makeQuery(id+"F0.imprint","IMPRINT",EDGE,{"derivedFrom":sQuery(id+"F0.wireOp",EDGE,"E17.sketch_text.stroke-660")}),-1.0]])]});
            var Q51;
            Q51=makeQuery(id+"F0.imprint","IMPRINT",FACE,{"disambiguationData":[TD([[makeQuery(id+"F0.imprint","IMPRINT",EDGE,{"derivedFrom":sQuery(id+"F0.wireOp",EDGE,"E17.sketch_text.stroke-405")}),-1.0]])]});
            var Q52;
            Q52=makeQuery(id+"F0.imprint","IMPRINT",FACE,{"disambiguationData":[TD([[makeQuery(id+"F0.imprint","IMPRINT",EDGE,{"derivedFrom":sQuery(id+"F0.wireOp",EDGE,"E17.sketch_text.stroke-1149")}),-1.0]])]});
            var Q53;
            Q53=makeQuery(id+"F0.imprint","IMPRINT",FACE,{"disambiguationData":[TD([[makeQuery(id+"F0.imprint","IMPRINT",EDGE,{"derivedFrom":sQuery(id+"F0.wireOp",EDGE,"E17.sketch_text.stroke-932")}),-1.0]])]});
            var Q54;
            Q54=makeQuery(id+"F0.imprint","IMPRINT",FACE,{"disambiguationData":[TD([[makeQuery(id+"F0.imprint","IMPRINT",EDGE,{"derivedFrom":sQuery(id+"F0.wireOp",EDGE,"E17.sketch_text.stroke-674")}),-1.0]])]});
            var Q55;
            Q55=makeQuery(id+"F0.imprint","IMPRINT",FACE,{"disambiguationData":[TD([[makeQuery(id+"F0.imprint","IMPRINT",EDGE,{"derivedFrom":sQuery(id+"F0.wireOp",EDGE,"E17.sketch_text.stroke-411")}),-1.0]])]});
            var Q56;
            Q56=makeQuery(id+"F0.imprint","IMPRINT",FACE,{"disambiguationData":[TD([[makeQuery(id+"F0.imprint","IMPRINT",EDGE,{"derivedFrom":sQuery(id+"F0.wireOp",EDGE,"E17.sketch_text.stroke-1165")}),-1.0]])]});
            var Q57;
            Q57=makeQuery(id+"F0.imprint","IMPRINT",FACE,{"disambiguationData":[TD([[makeQuery(id+"F0.imprint","IMPRINT",EDGE,{"derivedFrom":sQuery(id+"F0.wireOp",EDGE,"E17.sketch_text.stroke-693")}),-1.0]])]});
            var Q58;
            Q58=makeQuery(id+"F0.imprint","IMPRINT",FACE,{"disambiguationData":[TD([[makeQuery(id+"F0.imprint","IMPRINT",EDGE,{"derivedFrom":sQuery(id+"F0.wireOp",EDGE,"E17.sketch_text.stroke-420")}),-1.0]])]});
            var Q59;
            Q59=makeQuery(id+"F0.imprint","IMPRINT",FACE,{"disambiguationData":[TD([[makeQuery(id+"F0.imprint","IMPRINT",EDGE,{"derivedFrom":sQuery(id+"F0.wireOp",EDGE,"E17.sketch_text.stroke-230")}),-1.0]])]});
            var Q60;
            Q60=makeQuery(id+"F0.imprint","IMPRINT",FACE,{"disambiguationData":[TD([[makeQuery(id+"F0.imprint","IMPRINT",EDGE,{"derivedFrom":sQuery(id+"F0.wireOp",EDGE,"E17.sketch_text.stroke-955")}),-1.0]])]});
            var Q61;
            Q61=makeQuery(id+"F0.imprint","IMPRINT",FACE,{"disambiguationData":[TD([[makeQuery(id+"F0.imprint","IMPRINT",EDGE,{"derivedFrom":sQuery(id+"F0.wireOp",EDGE,"E17.sketch_text.stroke-1181")}),-1.0]])]});
            var Q62;
            Q62=makeQuery(id+"F0.imprint","IMPRINT",FACE,{"disambiguationData":[TD([[makeQuery(id+"F0.imprint","IMPRINT",EDGE,{"derivedFrom":sQuery(id+"F0.wireOp",EDGE,"E17.sketch_text.stroke-729")}),-1.0]])]});
            var Q63;
            Q63=makeQuery(id+"F0.imprint","IMPRINT",FACE,{"disambiguationData":[TD([[makeQuery(id+"F0.imprint","IMPRINT",EDGE,{"derivedFrom":sQuery(id+"F0.wireOp",EDGE,"E17.sketch_text.stroke-434")}),-1.0]])]});
            var Q64;
            Q64=makeQuery(id+"F0.imprint","IMPRINT",FACE,{"disambiguationData":[TD([[makeQuery(id+"F0.imprint","IMPRINT",EDGE,{"derivedFrom":sQuery(id+"F0.wireOp",EDGE,"E17.sketch_text.stroke-243")}),-1.0]])]});
            var Q65;
            Q65=makeQuery(id+"F0.imprint","IMPRINT",FACE,{"disambiguationData":[TD([[makeQuery(id+"F0.imprint","IMPRINT",EDGE,{"derivedFrom":sQuery(id+"F0.wireOp",EDGE,"E17.sketch_text.stroke-1188")}),-1.0]])]});
            var Q66;
            Q66=makeQuery(id+"F0.imprint","IMPRINT",FACE,{"disambiguationData":[TD([[makeQuery(id+"F0.imprint","IMPRINT",EDGE,{"derivedFrom":sQuery(id+"F0.wireOp",EDGE,"E17.sketch_text.stroke-959")}),-1.0]])]});
            var Q67;
            Q67=makeQuery(id+"F0.imprint","IMPRINT",FACE,{"disambiguationData":[TD([[makeQuery(id+"F0.imprint","IMPRINT",EDGE,{"derivedFrom":sQuery(id+"F0.wireOp",EDGE,"E17.sketch_text.stroke-733")}),-1.0]])]});
            var Q68;
            Q68=makeQuery(id+"F0.imprint","IMPRINT",FACE,{"disambiguationData":[TD([[makeQuery(id+"F0.imprint","IMPRINT",EDGE,{"derivedFrom":sQuery(id+"F0.wireOp",EDGE,"E17.sketch_text.stroke-459")}),-1.0]])]});
            var Q69;
            Q69=makeQuery(id+"F0.imprint","IMPRINT",FACE,{"disambiguationData":[TD([[makeQuery(id+"F0.imprint","IMPRINT",EDGE,{"derivedFrom":sQuery(id+"F0.wireOp",EDGE,"E17.sketch_text.stroke-1192")}),-1.0]])]});
            var Q70;
            Q70=makeQuery(id+"F0.imprint","IMPRINT",FACE,{"disambiguationData":[TD([[makeQuery(id+"F0.imprint","IMPRINT",EDGE,{"derivedFrom":sQuery(id+"F0.wireOp",EDGE,"E17.sketch_text.stroke-964")}),-1.0]])]});
            var Q71;
            Q71=makeQuery(id+"F0.imprint","IMPRINT",FACE,{"disambiguationData":[TD([[makeQuery(id+"F0.imprint","IMPRINT",EDGE,{"derivedFrom":sQuery(id+"F0.wireOp",EDGE,"E17.sketch_text.stroke-755")}),-1.0]])]});
            var Q72;
            Q72=makeQuery(id+"F0.imprint","IMPRINT",FACE,{"disambiguationData":[TD([[makeQuery(id+"F0.imprint","IMPRINT",EDGE,{"derivedFrom":sQuery(id+"F0.wireOp",EDGE,"E17.sketch_text.stroke-463")}),-1.0]])]});
            var Q73;
            Q73=makeQuery(id+"F0.imprint","IMPRINT",FACE,{"disambiguationData":[TD([[makeQuery(id+"F0.imprint","IMPRINT",EDGE,{"derivedFrom":sQuery(id+"F0.wireOp",EDGE,"E17.sketch_text.stroke-267")}),-1.0]])]});
            var Q74;
            Q74=makeQuery(id+"F0.imprint","IMPRINT",FACE,{"disambiguationData":[TD([[makeQuery(id+"F0.imprint","IMPRINT",EDGE,{"derivedFrom":sQuery(id+"F0.wireOp",EDGE,"E17.sketch_text.stroke-773")}),-1.0]])]});
            var Q75;
            Q75=makeQuery(id+"F0.imprint","IMPRINT",FACE,{"disambiguationData":[TD([[makeQuery(id+"F0.imprint","IMPRINT",EDGE,{"derivedFrom":sQuery(id+"F0.wireOp",EDGE,"E17.sketch_text.stroke-471")}),-1.0]])]});
            var Q76;
            Q76=makeQuery(id+"F0.imprint","IMPRINT",FACE,{"disambiguationData":[TD([[makeQuery(id+"F0.imprint","IMPRINT",EDGE,{"derivedFrom":sQuery(id+"F0.wireOp",EDGE,"E17.sketch_text.stroke-272")}),-1.0]])]});
            var Q77;
            Q77=makeQuery(id+"F0.imprint","IMPRINT",FACE,{"disambiguationData":[TD([[makeQuery(id+"F0.imprint","IMPRINT",EDGE,{"derivedFrom":sQuery(id+"F0.wireOp",EDGE,"E17.sketch_text.stroke-1205")}),-1.0]])]});
            var Q78;
            Q78=makeQuery(id+"F0.imprint","IMPRINT",FACE,{"disambiguationData":[TD([[makeQuery(id+"F0.imprint","IMPRINT",EDGE,{"derivedFrom":sQuery(id+"F0.wireOp",EDGE,"E17.sketch_text.stroke-989")}),-1.0]])]});
            var Q79;
            Q79=makeQuery(id+"F0.imprint","IMPRINT",FACE,{"disambiguationData":[TD([[makeQuery(id+"F0.imprint","IMPRINT",EDGE,{"derivedFrom":sQuery(id+"F0.wireOp",EDGE,"E17.sketch_text.stroke-497")}),-1.0]])]});
            var Q80;
            Q80=makeQuery(id+"F0.imprint","IMPRINT",FACE,{"disambiguationData":[TD([[makeQuery(id+"F0.imprint","IMPRINT",EDGE,{"derivedFrom":sQuery(id+"F0.wireOp",EDGE,"E17.sketch_text.stroke-1229")}),-1.0]])]});
            var Q81;
            Q81=makeQuery(id+"F0.imprint","IMPRINT",FACE,{"disambiguationData":[TD([[makeQuery(id+"F0.imprint","IMPRINT",EDGE,{"derivedFrom":sQuery(id+"F0.wireOp",EDGE,"E17.sketch_text.stroke-1002")}),-1.0]])]});
            var Q82;
            Q82=makeQuery(id+"F0.imprint","IMPRINT",FACE,{"disambiguationData":[TD([[makeQuery(id+"F0.imprint","IMPRINT",EDGE,{"derivedFrom":sQuery(id+"F0.wireOp",EDGE,"E17.sketch_text.stroke-828")}),-1.0]])]});
            var Q83;
            Q83=makeQuery(id+"F0.imprint","IMPRINT",FACE,{"disambiguationData":[TD([[makeQuery(id+"F0.imprint","IMPRINT",EDGE,{"derivedFrom":sQuery(id+"F0.wireOp",EDGE,"E17.sketch_text.stroke-514")}),-1.0]])]});
            var Q84;
            Q84=makeQuery(id+"F0.imprint","IMPRINT",FACE,{"disambiguationData":[TD([[makeQuery(id+"F0.imprint","IMPRINT",EDGE,{"derivedFrom":sQuery(id+"F0.wireOp",EDGE,"E17.sketch_text.stroke-316")}),-1.0]])]});
            var Q85;
            Q85=makeQuery(id+"F0.imprint","IMPRINT",FACE,{"disambiguationData":[TD([[makeQuery(id+"F0.imprint","IMPRINT",EDGE,{"derivedFrom":sQuery(id+"F0.wireOp",EDGE,"E17.sketch_text.stroke-1234")}),-1.0]])]});
            var Q86;
            Q86=makeQuery(id+"F0.imprint","IMPRINT",FACE,{"disambiguationData":[TD([[makeQuery(id+"F0.imprint","IMPRINT",EDGE,{"derivedFrom":sQuery(id+"F0.wireOp",EDGE,"E17.sketch_text.stroke-1026")}),-1.0]])]});
            var Q87;
            Q87=makeQuery(id+"F0.imprint","IMPRINT",FACE,{"disambiguationData":[TD([[makeQuery(id+"F0.imprint","IMPRINT",EDGE,{"derivedFrom":sQuery(id+"F0.wireOp",EDGE,"E17.sketch_text.stroke-852")}),-1.0]])]});
            var Q88;
            Q88=makeQuery(id+"F0.imprint","IMPRINT",FACE,{"disambiguationData":[TD([[makeQuery(id+"F0.imprint","IMPRINT",EDGE,{"derivedFrom":sQuery(id+"F0.wireOp",EDGE,"E17.sketch_text.stroke-533")}),-1.0]])]});
            var Q89;
            Q89=makeQuery(id+"F0.imprint","IMPRINT",FACE,{"disambiguationData":[TD([[makeQuery(id+"F0.imprint","IMPRINT",EDGE,{"derivedFrom":sQuery(id+"F0.wireOp",EDGE,"E17.sketch_text.stroke-320")}),-1.0]])]});
            var Q90;
            Q90=makeQuery(id+"F0.imprint","IMPRINT",FACE,{"disambiguationData":[TD([[makeQuery(id+"F0.imprint","IMPRINT",EDGE,{"derivedFrom":sQuery(id+"F0.wireOp",EDGE,"E17.sketch_text.stroke-908")}),-1.0]])]});
            extrude(context, id + "F2", {"entities" : qUnion([Q0, Q1, Q2, Q3, Q4, Q5, Q6, Q7, Q8, Q9, Q10, Q11, Q12, Q13, Q14, Q15, Q16, Q17, Q18, Q19, Q20, Q21, Q22, Q23, Q24, Q25, Q26, Q27, Q28, Q29, Q30, Q31, Q32, Q33, Q34, Q35, Q36, Q37, Q38, Q39, Q40, Q41, Q42, Q43, Q44, Q45, Q46, Q47, Q48, Q49, Q50, Q51, Q52, Q53, Q54, Q55, Q56, Q57, Q58, Q59, Q60, Q61, Q62, Q63, Q64, Q65, Q66, Q67, Q68, Q69, Q70, Q71, Q72, Q73, Q74, Q75, Q76, Q77, Q78, Q79, Q80, Q81, Q82, Q83, Q84, Q85, Q86, Q87, Q88, Q89, Q90]), "operationType" : NewBodyOperationType.ADD, "depth" : .2 * mm, "offsetDistance" : 25 * mm});
        }
        {
            var Q0;
            {var subQ0=sQuery(id+"F0.wireOp",EDGE,"E13");Q0=makeQuery(id+"F0.imprint","IMPRINT",FACE,{"disambiguationData":[TD([[makeQuery(id+"F0.imprint","IMPRINT",EDGE,{"derivedFrom":subQ0}),-1.0]])]});}
            var Q1;
            Q1=makeQuery(id+"F0.imprint","IMPRINT",FACE,{"disambiguationData":[TD([[makeQuery(id+"F0.imprint","IMPRINT",EDGE,{"derivedFrom":sQuery(id+"F0.wireOp",EDGE,"E11.0")}),-1.0]])]});
            var Q2;
            Q2=makeQuery(id+"F0.imprint","IMPRINT",FACE,{"disambiguationData":[TD([[makeQuery(id+"F0.imprint","IMPRINT",EDGE,{"derivedFrom":sQuery(id+"F0.wireOp",EDGE,"E17.sketch_text.stroke-852")}),-1.0]])]});
            var Q3;
            Q3=makeQuery(id+"F0.imprint","IMPRINT",FACE,{"disambiguationData":[TD([[makeQuery(id+"F0.imprint","IMPRINT",EDGE,{"derivedFrom":sQuery(id+"F0.wireOp",EDGE,"E17.sketch_text.stroke-159")}),-1.0]])]});
            var Q4;
            Q4=makeQuery(id+"F0.imprint","IMPRINT",FACE,{"disambiguationData":[TD([[makeQuery(id+"F0.imprint","IMPRINT",EDGE,{"derivedFrom":sQuery(id+"F0.wireOp",EDGE,"E17.sketch_text.stroke-243")}),-1.0]])]});
            var Q5;
            Q5=makeQuery(id+"F0.imprint","IMPRINT",FACE,{"disambiguationData":[TD([[makeQuery(id+"F0.imprint","IMPRINT",EDGE,{"derivedFrom":sQuery(id+"F0.wireOp",EDGE,"E17.sketch_text.stroke-729")}),-1.0]])]});
            var Q6;
            Q6=makeQuery(id+"F0.imprint","IMPRINT",FACE,{"disambiguationData":[TD([[makeQuery(id+"F0.imprint","IMPRINT",EDGE,{"derivedFrom":sQuery(id+"F0.wireOp",EDGE,"E17.sketch_text.stroke-344")}),-1.0]])]});
            var Q7;
            Q7=makeQuery(id+"F0.imprint","IMPRINT",FACE,{"disambiguationData":[TD([[makeQuery(id+"F0.imprint","IMPRINT",EDGE,{"derivedFrom":sQuery(id+"F0.wireOp",EDGE,"E17.sketch_text.stroke-1026")}),-1.0]])]});
            var Q8;
            Q8=makeQuery(id+"F0.imprint","IMPRINT",FACE,{"disambiguationData":[TD([[makeQuery(id+"F0.imprint","IMPRINT",EDGE,{"derivedFrom":sQuery(id+"F0.wireOp",EDGE,"E17.sketch_text.stroke-165")}),-1.0]])]});
            var Q9;
            Q9=makeQuery(id+"F0.imprint","IMPRINT",FACE,{"disambiguationData":[TD([[makeQuery(id+"F0.imprint","IMPRINT",EDGE,{"derivedFrom":sQuery(id+"F0.wireOp",EDGE,"E17.sketch_text.stroke-174")}),-1.0]])]});
            var Q10;
            Q10=makeQuery(id+"F0.imprint","IMPRINT",FACE,{"disambiguationData":[TD([[makeQuery(id+"F0.imprint","IMPRINT",EDGE,{"derivedFrom":sQuery(id+"F0.wireOp",EDGE,"E17.sketch_text.stroke-894")}),-1.0]])]});
            var Q11;
            Q11=makeQuery(id+"F0.imprint","IMPRINT",FACE,{"disambiguationData":[TD([[makeQuery(id+"F0.imprint","IMPRINT",EDGE,{"derivedFrom":sQuery(id+"F0.wireOp",EDGE,"E17.sketch_text.stroke-121")}),-1.0]])]});
            var Q12;
            Q12=makeQuery(id+"F0.imprint","IMPRINT",FACE,{"disambiguationData":[TD([[makeQuery(id+"F0.imprint","IMPRINT",EDGE,{"derivedFrom":sQuery(id+"F0.wireOp",EDGE,"E17.sketch_text.stroke-463")}),-1.0]])]});
            var Q13;
            Q13=makeQuery(id+"F0.imprint","IMPRINT",FACE,{"disambiguationData":[TD([[makeQuery(id+"F0.imprint","IMPRINT",EDGE,{"derivedFrom":sQuery(id+"F0.wireOp",EDGE,"E17.sketch_text.stroke-471")}),-1.0]])]});
            var Q14;
            Q14=makeQuery(id+"F0.imprint","IMPRINT",FACE,{"disambiguationData":[TD([[makeQuery(id+"F0.imprint","IMPRINT",EDGE,{"derivedFrom":sQuery(id+"F0.wireOp",EDGE,"E17.sketch_text.stroke-1181")}),-1.0]])]});
            var Q15;
            Q15=makeQuery(id+"F0.imprint","IMPRINT",FACE,{"disambiguationData":[TD([[makeQuery(id+"F0.imprint","IMPRINT",EDGE,{"derivedFrom":sQuery(id+"F0.wireOp",EDGE,"E17.sketch_text.stroke-1192")}),-1.0]])]});
            var Q16;
            Q16=makeQuery(id+"F0.imprint","IMPRINT",FACE,{"disambiguationData":[TD([[makeQuery(id+"F0.imprint","IMPRINT",EDGE,{"derivedFrom":sQuery(id+"F0.wireOp",EDGE,"E17.sketch_text.stroke-674")}),-1.0]])]});
            var Q17;
            Q17=makeQuery(id+"F0.imprint","IMPRINT",FACE,{"disambiguationData":[TD([[makeQuery(id+"F0.imprint","IMPRINT",EDGE,{"derivedFrom":sQuery(id+"F0.wireOp",EDGE,"E17.sketch_text.stroke-108")}),-1.0]])]});
            var Q18;
            Q18=makeQuery(id+"F0.imprint","IMPRINT",FACE,{"disambiguationData":[TD([[makeQuery(id+"F0.imprint","IMPRINT",EDGE,{"derivedFrom":sQuery(id+"F0.wireOp",EDGE,"E17.sketch_text.stroke-792")}),-1.0]])]});
            var Q19;
            Q19=makeQuery(id+"F0.imprint","IMPRINT",FACE,{"disambiguationData":[TD([[makeQuery(id+"F0.imprint","IMPRINT",EDGE,{"derivedFrom":sQuery(id+"F0.wireOp",EDGE,"E17.sketch_text.stroke-267")}),-1.0]])]});
            var Q20;
            Q20=makeQuery(id+"F0.imprint","IMPRINT",FACE,{"disambiguationData":[TD([[makeQuery(id+"F0.imprint","IMPRINT",EDGE,{"derivedFrom":sQuery(id+"F0.wireOp",EDGE,"E17.sketch_text.stroke-645")}),-1.0]])]});
            var Q21;
            Q21=makeQuery(id+"F0.imprint","IMPRINT",FACE,{"disambiguationData":[TD([[makeQuery(id+"F0.imprint","IMPRINT",EDGE,{"derivedFrom":sQuery(id+"F0.wireOp",EDGE,"E17.sketch_text.stroke-145")}),-1.0]])]});
            var Q22;
            Q22=makeQuery(id+"F0.imprint","IMPRINT",FACE,{"disambiguationData":[TD([[makeQuery(id+"F0.imprint","IMPRINT",EDGE,{"derivedFrom":sQuery(id+"F0.wireOp",EDGE,"E17.sketch_text.stroke-31")}),-1.0]])]});
            var Q23;
            Q23=makeQuery(id+"F0.imprint","IMPRINT",FACE,{"disambiguationData":[TD([[makeQuery(id+"F0.imprint","IMPRINT",EDGE,{"derivedFrom":sQuery(id+"F0.wireOp",EDGE,"E17.sketch_text.stroke-1087")}),-1.0]])]});
            var Q24;
            Q24=makeQuery(id+"F0.imprint","IMPRINT",FACE,{"disambiguationData":[TD([[makeQuery(id+"F0.imprint","IMPRINT",EDGE,{"derivedFrom":sQuery(id+"F0.wireOp",EDGE,"E17.sketch_text.stroke-72")}),-1.0]])]});
            var Q25;
            Q25=makeQuery(id+"F0.imprint","IMPRINT",FACE,{"disambiguationData":[TD([[makeQuery(id+"F0.imprint","IMPRINT",EDGE,{"derivedFrom":sQuery(id+"F0.wireOp",EDGE,"E17.sketch_text.stroke-901")}),-1.0]])]});
            var Q26;
            Q26=makeQuery(id+"F0.imprint","IMPRINT",FACE,{"disambiguationData":[TD([[makeQuery(id+"F0.imprint","IMPRINT",EDGE,{"derivedFrom":sQuery(id+"F0.wireOp",EDGE,"E17.sketch_text.stroke-411")}),-1.0]])]});
            var Q27;
            Q27=makeQuery(id+"F0.imprint","IMPRINT",FACE,{"disambiguationData":[TD([[makeQuery(id+"F0.imprint","IMPRINT",EDGE,{"derivedFrom":sQuery(id+"F0.wireOp",EDGE,"E17.sketch_text.stroke-932")}),-1.0]])]});
            var Q28;
            Q28=makeQuery(id+"F0.imprint","IMPRINT",FACE,{"disambiguationData":[TD([[makeQuery(id+"F0.imprint","IMPRINT",EDGE,{"derivedFrom":sQuery(id+"F0.wireOp",EDGE,"E17.sketch_text.stroke-325")}),-1.0]])]});
            var Q29;
            Q29=makeQuery(id+"F0.imprint","IMPRINT",FACE,{"disambiguationData":[TD([[makeQuery(id+"F0.imprint","IMPRINT",EDGE,{"derivedFrom":sQuery(id+"F0.wireOp",EDGE,"E17.sketch_text.stroke-94")}),-1.0]])]});
            var Q30;
            Q30=makeQuery(id+"F0.imprint","IMPRINT",FACE,{"disambiguationData":[TD([[makeQuery(id+"F0.imprint","IMPRINT",EDGE,{"derivedFrom":sQuery(id+"F0.wireOp",EDGE,"E17.sketch_text.stroke-349")}),-1.0]])]});
            var Q31;
            Q31=makeQuery(id+"F0.imprint","IMPRINT",FACE,{"disambiguationData":[TD([[makeQuery(id+"F0.imprint","IMPRINT",EDGE,{"derivedFrom":sQuery(id+"F0.wireOp",EDGE,"E17.sketch_text.stroke-1112")}),-1.0]])]});
            var Q32;
            Q32=makeQuery(id+"F0.imprint","IMPRINT",FACE,{"disambiguationData":[TD([[makeQuery(id+"F0.imprint","IMPRINT",EDGE,{"derivedFrom":sQuery(id+"F0.wireOp",EDGE,"E17.sketch_text.stroke-272")}),-1.0]])]});
            var Q33;
            Q33=makeQuery(id+"F0.imprint","IMPRINT",FACE,{"disambiguationData":[TD([[makeQuery(id+"F0.imprint","IMPRINT",EDGE,{"derivedFrom":sQuery(id+"F0.wireOp",EDGE,"E17.sketch_text.stroke-44")}),-1.0]])]});
            var Q34;
            Q34=makeQuery(id+"F0.imprint","IMPRINT",FACE,{"disambiguationData":[TD([[makeQuery(id+"F0.imprint","IMPRINT",EDGE,{"derivedFrom":sQuery(id+"F0.wireOp",EDGE,"E17.sketch_text.stroke-607")}),-1.0]])]});
            var Q35;
            Q35=makeQuery(id+"F0.imprint","IMPRINT",FACE,{"disambiguationData":[TD([[makeQuery(id+"F0.imprint","IMPRINT",EDGE,{"derivedFrom":sQuery(id+"F0.wireOp",EDGE,"E17.sketch_text.stroke-908")}),-1.0]])]});
            var Q36;
            Q36=makeQuery(id+"F0.imprint","IMPRINT",FACE,{"disambiguationData":[TD([[makeQuery(id+"F0.imprint","IMPRINT",EDGE,{"derivedFrom":sQuery(id+"F0.wireOp",EDGE,"E17.sketch_text.stroke-1149")}),-1.0]])]});
            var Q37;
            Q37=makeQuery(id+"F0.imprint","IMPRINT",FACE,{"disambiguationData":[TD([[makeQuery(id+"F0.imprint","IMPRINT",EDGE,{"derivedFrom":sQuery(id+"F0.wireOp",EDGE,"E17.sketch_text.stroke-367")}),-1.0]])]});
            var Q38;
            Q38=makeQuery(id+"F0.imprint","IMPRINT",FACE,{"disambiguationData":[TD([[makeQuery(id+"F0.imprint","IMPRINT",EDGE,{"derivedFrom":sQuery(id+"F0.wireOp",EDGE,"E17.sketch_text.stroke-68")}),-1.0]])]});
            var Q39;
            Q39=makeQuery(id+"F0.imprint","IMPRINT",FACE,{"disambiguationData":[TD([[makeQuery(id+"F0.imprint","IMPRINT",EDGE,{"derivedFrom":sQuery(id+"F0.wireOp",EDGE,"E17.sketch_text.stroke-8")}),-1.0]])]});
            var Q40;
            Q40=makeQuery(id+"F0.imprint","IMPRINT",FACE,{"disambiguationData":[TD([[makeQuery(id+"F0.imprint","IMPRINT",EDGE,{"derivedFrom":sQuery(id+"F0.wireOp",EDGE,"E17.sketch_text.stroke-0")}),-1.0]])]});
            var Q41;
            Q41=makeQuery(id+"F0.imprint","IMPRINT",FACE,{"disambiguationData":[TD([[makeQuery(id+"F0.imprint","IMPRINT",EDGE,{"derivedFrom":sQuery(id+"F0.wireOp",EDGE,"E17.sketch_text.stroke-631")}),-1.0]])]});
            var Q42;
            Q42=makeQuery(id+"F0.imprint","IMPRINT",FACE,{"disambiguationData":[TD([[makeQuery(id+"F0.imprint","IMPRINT",EDGE,{"derivedFrom":sQuery(id+"F0.wireOp",EDGE,"E17.sketch_text.stroke-12")}),-1.0]])]});
            var Q43;
            Q43=makeQuery(id+"F0.imprint","IMPRINT",FACE,{"disambiguationData":[TD([[makeQuery(id+"F0.imprint","IMPRINT",EDGE,{"derivedFrom":sQuery(id+"F0.wireOp",EDGE,"E17.sketch_text.stroke-1079")}),-1.0]])]});
            var Q44;
            Q44=makeQuery(id+"F0.imprint","IMPRINT",FACE,{"disambiguationData":[TD([[makeQuery(id+"F0.imprint","IMPRINT",EDGE,{"derivedFrom":sQuery(id+"F0.wireOp",EDGE,"E17.sketch_text.stroke-405")}),-1.0]])]});
            var Q45;
            Q45=makeQuery(id+"F0.imprint","IMPRINT",FACE,{"disambiguationData":[TD([[makeQuery(id+"F0.imprint","IMPRINT",EDGE,{"derivedFrom":sQuery(id+"F0.wireOp",EDGE,"E17.sketch_text.stroke-660")}),-1.0]])]});
            var Q46;
            Q46=makeQuery(id+"F0.imprint","IMPRINT",FACE,{"disambiguationData":[TD([[makeQuery(id+"F0.imprint","IMPRINT",EDGE,{"derivedFrom":sQuery(id+"F0.wireOp",EDGE,"E17.sketch_text.stroke-926")}),-1.0]])]});
            var Q47;
            Q47=makeQuery(id+"F0.imprint","IMPRINT",FACE,{"disambiguationData":[TD([[makeQuery(id+"F0.imprint","IMPRINT",EDGE,{"derivedFrom":sQuery(id+"F0.wireOp",EDGE,"E17.sketch_text.stroke-1141")}),-1.0]])]});
            var Q48;
            Q48=makeQuery(id+"F0.imprint","IMPRINT",FACE,{"disambiguationData":[TD([[makeQuery(id+"F0.imprint","IMPRINT",EDGE,{"derivedFrom":sQuery(id+"F0.wireOp",EDGE,"E17.sketch_text.stroke-391")}),-1.0]])]});
            var Q49;
            Q49=makeQuery(id+"F0.imprint","IMPRINT",FACE,{"disambiguationData":[TD([[makeQuery(id+"F0.imprint","IMPRINT",EDGE,{"derivedFrom":sQuery(id+"F0.wireOp",EDGE,"E17.sketch_text.stroke-354")}),-1.0]])]});
            var Q50;
            Q50=makeQuery(id+"F0.imprint","IMPRINT",FACE,{"disambiguationData":[TD([[makeQuery(id+"F0.imprint","IMPRINT",EDGE,{"derivedFrom":sQuery(id+"F0.wireOp",EDGE,"E17.sketch_text.stroke-1188")}),-1.0]])]});
            var Q51;
            Q51=makeQuery(id+"F0.imprint","IMPRINT",FACE,{"disambiguationData":[TD([[makeQuery(id+"F0.imprint","IMPRINT",EDGE,{"derivedFrom":sQuery(id+"F0.wireOp",EDGE,"E17.sketch_text.stroke-959")}),-1.0]])]});
            var Q52;
            Q52=makeQuery(id+"F0.imprint","IMPRINT",FACE,{"disambiguationData":[TD([[makeQuery(id+"F0.imprint","IMPRINT",EDGE,{"derivedFrom":sQuery(id+"F0.wireOp",EDGE,"E17.sketch_text.stroke-434")}),-1.0]])]});
            var Q53;
            Q53=makeQuery(id+"F0.imprint","IMPRINT",FACE,{"disambiguationData":[TD([[makeQuery(id+"F0.imprint","IMPRINT",EDGE,{"derivedFrom":sQuery(id+"F0.wireOp",EDGE,"E17.sketch_text.stroke-230")}),-1.0]])]});
            var Q54;
            Q54=makeQuery(id+"F0.imprint","IMPRINT",FACE,{"disambiguationData":[TD([[makeQuery(id+"F0.imprint","IMPRINT",EDGE,{"derivedFrom":sQuery(id+"F0.wireOp",EDGE,"E17.sketch_text.stroke-420")}),-1.0]])]});
            var Q55;
            Q55=makeQuery(id+"F0.imprint","IMPRINT",FACE,{"disambiguationData":[TD([[makeQuery(id+"F0.imprint","IMPRINT",EDGE,{"derivedFrom":sQuery(id+"F0.wireOp",EDGE,"E17.sketch_text.stroke-205")}),-1.0]])]});
            var Q56;
            Q56=makeQuery(id+"F0.imprint","IMPRINT",FACE,{"disambiguationData":[TD([[makeQuery(id+"F0.imprint","IMPRINT",EDGE,{"derivedFrom":sQuery(id+"F0.wireOp",EDGE,"E17.sketch_text.stroke-941")}),-1.0]])]});
            var Q57;
            Q57=makeQuery(id+"F0.imprint","IMPRINT",FACE,{"disambiguationData":[TD([[makeQuery(id+"F0.imprint","IMPRINT",EDGE,{"derivedFrom":sQuery(id+"F0.wireOp",EDGE,"E17.sketch_text.stroke-870")}),-1.0]])]});
            var Q58;
            Q58=makeQuery(id+"F0.imprint","IMPRINT",FACE,{"disambiguationData":[TD([[makeQuery(id+"F0.imprint","IMPRINT",EDGE,{"derivedFrom":sQuery(id+"F0.wireOp",EDGE,"E17.sketch_text.stroke-857")}),-1.0]])]});
            var Q59;
            Q59=makeQuery(id+"F0.imprint","IMPRINT",FACE,{"disambiguationData":[TD([[makeQuery(id+"F0.imprint","IMPRINT",EDGE,{"derivedFrom":sQuery(id+"F0.wireOp",EDGE,"E17.sketch_text.stroke-569")}),-1.0]])]});
            var Q60;
            Q60=makeQuery(id+"F0.imprint","IMPRINT",FACE,{"disambiguationData":[TD([[makeQuery(id+"F0.imprint","IMPRINT",EDGE,{"derivedFrom":sQuery(id+"F0.wireOp",EDGE,"E17.sketch_text.stroke-533")}),-1.0]])]});
            var Q61;
            Q61=makeQuery(id+"F0.imprint","IMPRINT",FACE,{"disambiguationData":[TD([[makeQuery(id+"F0.imprint","IMPRINT",EDGE,{"derivedFrom":sQuery(id+"F0.wireOp",EDGE,"E17.sketch_text.stroke-1234")}),-1.0]])]});
            var Q62;
            Q62=makeQuery(id+"F0.imprint","IMPRINT",FACE,{"disambiguationData":[TD([[makeQuery(id+"F0.imprint","IMPRINT",EDGE,{"derivedFrom":sQuery(id+"F0.wireOp",EDGE,"E17.sketch_text.stroke-594")}),-1.0]])]});
            var Q63;
            Q63=makeQuery(id+"F0.imprint","IMPRINT",FACE,{"disambiguationData":[TD([[makeQuery(id+"F0.imprint","IMPRINT",EDGE,{"derivedFrom":sQuery(id+"F0.wireOp",EDGE,"E17.sketch_text.stroke-773")}),-1.0]])]});
            var Q64;
            Q64=makeQuery(id+"F0.imprint","IMPRINT",FACE,{"disambiguationData":[TD([[makeQuery(id+"F0.imprint","IMPRINT",EDGE,{"derivedFrom":sQuery(id+"F0.wireOp",EDGE,"E17.sketch_text.stroke-1205")}),-1.0]])]});
            var Q65;
            Q65=makeQuery(id+"F0.imprint","IMPRINT",FACE,{"disambiguationData":[TD([[makeQuery(id+"F0.imprint","IMPRINT",EDGE,{"derivedFrom":sQuery(id+"F0.wireOp",EDGE,"E17.sketch_text.stroke-755")}),-1.0]])]});
            var Q66;
            Q66=makeQuery(id+"F0.imprint","IMPRINT",FACE,{"disambiguationData":[TD([[makeQuery(id+"F0.imprint","IMPRINT",EDGE,{"derivedFrom":sQuery(id+"F0.wireOp",EDGE,"E17.sketch_text.stroke-514")}),-1.0]])]});
            var Q67;
            Q67=makeQuery(id+"F0.imprint","IMPRINT",FACE,{"disambiguationData":[TD([[makeQuery(id+"F0.imprint","IMPRINT",EDGE,{"derivedFrom":sQuery(id+"F0.wireOp",EDGE,"E17.sketch_text.stroke-1002")}),-1.0]])]});
            var Q68;
            Q68=makeQuery(id+"F0.imprint","IMPRINT",FACE,{"disambiguationData":[TD([[makeQuery(id+"F0.imprint","IMPRINT",EDGE,{"derivedFrom":sQuery(id+"F0.wireOp",EDGE,"E17.sketch_text.stroke-291")}),-1.0]])]});
            var Q69;
            Q69=makeQuery(id+"F0.imprint","IMPRINT",FACE,{"disambiguationData":[TD([[makeQuery(id+"F0.imprint","IMPRINT",EDGE,{"derivedFrom":sQuery(id+"F0.wireOp",EDGE,"E17.sketch_text.stroke-964")}),-1.0]])]});
            var Q70;
            Q70=makeQuery(id+"F0.imprint","IMPRINT",FACE,{"disambiguationData":[TD([[makeQuery(id+"F0.imprint","IMPRINT",EDGE,{"derivedFrom":sQuery(id+"F0.wireOp",EDGE,"E17.sketch_text.stroke-1165")}),-1.0]])]});
            var Q71;
            Q71=makeQuery(id+"F0.imprint","IMPRINT",FACE,{"disambiguationData":[TD([[makeQuery(id+"F0.imprint","IMPRINT",EDGE,{"derivedFrom":sQuery(id+"F0.wireOp",EDGE,"E17.sketch_text.stroke-1050")}),-1.0]])]});
            var Q72;
            Q72=makeQuery(id+"F0.imprint","IMPRINT",FACE,{"disambiguationData":[TD([[makeQuery(id+"F0.imprint","IMPRINT",EDGE,{"derivedFrom":sQuery(id+"F0.wireOp",EDGE,"E17.sketch_text.stroke-320")}),-1.0]])]});
            var Q73;
            Q73=makeQuery(id+"F0.imprint","IMPRINT",FACE,{"disambiguationData":[TD([[makeQuery(id+"F0.imprint","IMPRINT",EDGE,{"derivedFrom":sQuery(id+"F0.wireOp",EDGE,"E17.sketch_text.stroke-1075")}),-1.0]])]});
            var Q74;
            Q74=makeQuery(id+"F0.imprint","IMPRINT",FACE,{"disambiguationData":[TD([[makeQuery(id+"F0.imprint","IMPRINT",EDGE,{"derivedFrom":sQuery(id+"F0.wireOp",EDGE,"E17.sketch_text.stroke-316")}),-1.0]])]});
            var Q75;
            Q75=makeQuery(id+"F0.imprint","IMPRINT",FACE,{"disambiguationData":[TD([[makeQuery(id+"F0.imprint","IMPRINT",EDGE,{"derivedFrom":sQuery(id+"F0.wireOp",EDGE,"E17.sketch_text.stroke-497")}),-1.0]])]});
            var Q76;
            Q76=makeQuery(id+"F0.imprint","IMPRINT",FACE,{"disambiguationData":[TD([[makeQuery(id+"F0.imprint","IMPRINT",EDGE,{"derivedFrom":sQuery(id+"F0.wireOp",EDGE,"E17.sketch_text.stroke-200")}),-1.0]])]});
            var Q77;
            Q77=makeQuery(id+"F0.imprint","IMPRINT",FACE,{"disambiguationData":[TD([[makeQuery(id+"F0.imprint","IMPRINT",EDGE,{"derivedFrom":sQuery(id+"F0.wireOp",EDGE,"E17.sketch_text.stroke-912")}),-1.0]])]});
            var Q78;
            Q78=makeQuery(id+"F0.imprint","IMPRINT",FACE,{"disambiguationData":[TD([[makeQuery(id+"F0.imprint","IMPRINT",EDGE,{"derivedFrom":sQuery(id+"F0.wireOp",EDGE,"E17.sketch_text.stroke-188")}),-1.0]])]});
            var Q79;
            Q79=makeQuery(id+"F0.imprint","IMPRINT",FACE,{"disambiguationData":[TD([[makeQuery(id+"F0.imprint","IMPRINT",EDGE,{"derivedFrom":sQuery(id+"F0.wireOp",EDGE,"E17.sketch_text.stroke-651")}),-1.0]])]});
            var Q80;
            Q80=makeQuery(id+"F0.imprint","IMPRINT",FACE,{"disambiguationData":[TD([[makeQuery(id+"F0.imprint","IMPRINT",EDGE,{"derivedFrom":sQuery(id+"F0.wireOp",EDGE,"E17.sketch_text.stroke-1136")}),-1.0]])]});
            var Q81;
            Q81=makeQuery(id+"F0.imprint","IMPRINT",FACE,{"disambiguationData":[TD([[makeQuery(id+"F0.imprint","IMPRINT",EDGE,{"derivedFrom":sQuery(id+"F0.wireOp",EDGE,"E17.sketch_text.stroke-101")}),-1.0]])]});
            var Q82;
            Q82=makeQuery(id+"F0.imprint","IMPRINT",FACE,{"disambiguationData":[TD([[makeQuery(id+"F0.imprint","IMPRINT",EDGE,{"derivedFrom":sQuery(id+"F0.wireOp",EDGE,"E17.sketch_text.stroke-459")}),-1.0]])]});
            var Q83;
            Q83=makeQuery(id+"F0.imprint","IMPRINT",FACE,{"disambiguationData":[TD([[makeQuery(id+"F0.imprint","IMPRINT",EDGE,{"derivedFrom":sQuery(id+"F0.wireOp",EDGE,"E17.sketch_text.stroke-955")}),-1.0]])]});
            var Q84;
            Q84=makeQuery(id+"F0.imprint","IMPRINT",FACE,{"disambiguationData":[TD([[makeQuery(id+"F0.imprint","IMPRINT",EDGE,{"derivedFrom":sQuery(id+"F0.wireOp",EDGE,"E17.sketch_text.stroke-733")}),-1.0]])]});
            var Q85;
            Q85=makeQuery(id+"F0.imprint","IMPRINT",FACE,{"disambiguationData":[TD([[makeQuery(id+"F0.imprint","IMPRINT",EDGE,{"derivedFrom":sQuery(id+"F0.wireOp",EDGE,"E17.sketch_text.stroke-693")}),-1.0]])]});
            var Q86;
            Q86=makeQuery(id+"F0.imprint","IMPRINT",FACE,{"disambiguationData":[TD([[makeQuery(id+"F0.imprint","IMPRINT",EDGE,{"derivedFrom":sQuery(id+"F0.wireOp",EDGE,"E17.sketch_text.stroke-1031")}),-1.0]])]});
            var Q87;
            Q87=makeQuery(id+"F0.imprint","IMPRINT",FACE,{"disambiguationData":[TD([[makeQuery(id+"F0.imprint","IMPRINT",EDGE,{"derivedFrom":sQuery(id+"F0.wireOp",EDGE,"E17.sketch_text.stroke-989")}),-1.0]])]});
            var Q88;
            Q88=makeQuery(id+"F0.imprint","IMPRINT",FACE,{"disambiguationData":[TD([[makeQuery(id+"F0.imprint","IMPRINT",EDGE,{"derivedFrom":sQuery(id+"F0.wireOp",EDGE,"E17.sketch_text.stroke-828")}),-1.0]])]});
            var Q89;
            Q89=makeQuery(id+"F0.imprint","IMPRINT",FACE,{"disambiguationData":[TD([[makeQuery(id+"F0.imprint","IMPRINT",EDGE,{"derivedFrom":sQuery(id+"F0.wireOp",EDGE,"E17.sketch_text.stroke-1229")}),-1.0]])]});
            var Q90;
            Q90=makeQuery(id+"F0.imprint","IMPRINT",FACE,{"disambiguationData":[TD([[makeQuery(id+"F0.imprint","IMPRINT",EDGE,{"derivedFrom":sQuery(id+"F0.wireOp",EDGE,"E17.sketch_text.stroke-192")}),-1.0]])]});
            extrude(context, id + "F3", {"entities" : qUnion([Q0, Q1, Q2, Q3, Q4, Q5, Q6, Q7, Q8, Q9, Q10, Q11, Q12, Q13, Q14, Q15, Q16, Q17, Q18, Q19, Q20, Q21, Q22, Q23, Q24, Q25, Q26, Q27, Q28, Q29, Q30, Q31, Q32, Q33, Q34, Q35, Q36, Q37, Q38, Q39, Q40, Q41, Q42, Q43, Q44, Q45, Q46, Q47, Q48, Q49, Q50, Q51, Q52, Q53, Q54, Q55, Q56, Q57, Q58, Q59, Q60, Q61, Q62, Q63, Q64, Q65, Q66, Q67, Q68, Q69, Q70, Q71, Q72, Q73, Q74, Q75, Q76, Q77, Q78, Q79, Q80, Q81, Q82, Q83, Q84, Q85, Q86, Q87, Q88, Q89, Q90]), "depth" : 1 * mm, "hasSecondDirection" : true, "secondDirectionOppositeDirection" : true, "secondDirectionDepth" : -.2 * mm, "offsetDistance" : 25 * mm});
        }
    });
